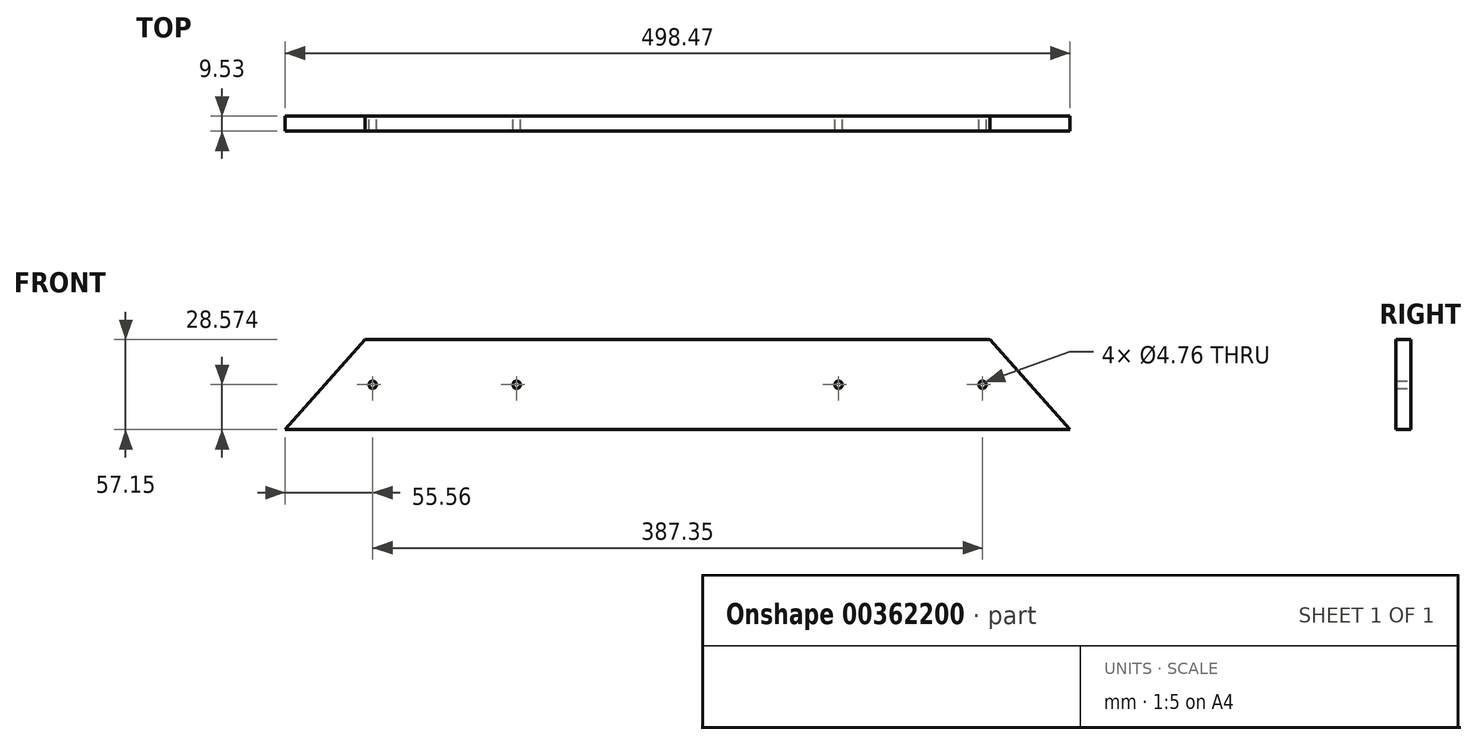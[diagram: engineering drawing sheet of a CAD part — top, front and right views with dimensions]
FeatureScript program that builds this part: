
annotation { "Feature Type Name" : "Feature", "Feature Type Description" : "" }
export const myFeature = defineFeature(function(context is Context, id is Id, definition is map)
    precondition{}
    {
        {
            var Q0;
            Q0=qCreatedBy(makeId("Front.planeOp"),FACE);
            var sketch = newSketch(context, id + "F0", { "sketchPlane" : qUnion([Q0])});
            skLineSegment(sketch, "E0.bottom", {"start": v(-185.67, -16.6) * mm, "end": v(211.2, -16.6) * mm});
            skLineSegment(sketch, "E0.top", {"start": v(-236.47, -73.75) * mm, "end": v(262, -73.75) * mm});
            skLineSegment(sketch, "E1", {"start": v(-236.47, -73.75) * mm, "end": v(-185.67, -16.6) * mm});
            skLineSegment(sketch, "E2", {"start": v(262, -73.75) * mm, "end": v(211.2, -16.6) * mm});
            skPoint(sketch, "E3.orphan", {"position": v(-211.39, -16.6) * mm});
            skPoint(sketch, "E0.right.start.orphan", {"position": v(261.69, -16.6) * mm});
            skLineSegment(sketch, "E4", {"start": v(211.2, -16.6) * mm, "end": v(211.2, -73.75) * mm, "construction": true});
            skLineSegment(sketch, "E5", {"start": v(211.2, -73.75) * mm, "end": v(119.13, -73.75) * mm});
            skLineSegment(sketch, "E6", {"start": v(-185.67, -16.6) * mm, "end": v(-185.67, -73.75) * mm, "construction": true});
            skLineSegment(sketch, "E7", {"start": v(-185.67, -73.75) * mm, "end": v(-93.6, -73.75) * mm});
            skLineSegment(sketch, "E8", {"start": v(119.13, -73.75) * mm, "end": v(119.13, -16.6) * mm, "construction": true});
            skLineSegment(sketch, "E9", {"start": v(-93.6, -73.75) * mm, "end": v(-93.6, -16.6) * mm, "construction": true});
            skPoint(sketch, "E10", {"position": v(119.13, -45.18) * mm});
            skPoint(sketch, "E11", {"position": v(-93.6, -45.18) * mm});
            skLineSegment(sketch, "E12", {"start": v(-176.15, -16.6) * mm, "end": v(-176.15, -73.75) * mm, "construction": true});
            skLineSegment(sketch, "E13", {"start": v(201.68, -16.6) * mm, "end": v(201.68, -73.75) * mm, "construction": true});
            skLineSegment(sketch, "E14", {"start": v(201.68, -45.18) * mm, "end": v(211.2, -45.18) * mm, "construction": true});
            skLineSegment(sketch, "E15", {"start": v(-185.67, -45.18) * mm, "end": v(-176.15, -45.18) * mm, "construction": true});
            skPoint(sketch, "E16", {"position": v(-180.91, -45.18) * mm});
            skLineSegment(sketch, "E17", {"start": v(110.87, -16.6) * mm, "end": v(110.87, -73.75) * mm, "construction": true});
            skLineSegment(sketch, "E18", {"start": v(-85.34, -16.6) * mm, "end": v(-85.34, -73.75) * mm, "construction": true});
            skLineSegment(sketch, "E19", {"start": v(-85.34, -45.18) * mm, "end": v(-93.6, -45.18) * mm, "construction": true});
            skLineSegment(sketch, "E20", {"start": v(119.13, -45.18) * mm, "end": v(110.87, -45.18) * mm, "construction": true});
            skPoint(sketch, "E21", {"position": v(115, -45.18) * mm});
            skPoint(sketch, "E22", {"position": v(-89.47, -45.18) * mm});
            skPoint(sketch, "E23", {"position": v(206.44, -45.18) * mm});
            skSolve(sketch);
        }
        {
            var Q0;
            Q0=makeQuery(id+"F0.imprint","IMPRINT",FACE,{"disambiguationData":[TD([[makeQuery(id+"F0.imprint","IMPRINT",EDGE,{"derivedFrom":sQuery(id+"F0.wireOp",EDGE,"E0.bottom")}),-1.0]])]});
            extrude(context, id + "F1", {"entities" : qUnion([Q0]), "depth" : 9.52 * mm});
        }
        {
            var Q0;
            Q0 = qSketchRegion(id + "F0", true);
            extrude(context, id + "F2", {"entities" : qUnion([Q0]), "operationType" : NewBodyOperationType.ADD, "depth" : 9.52 * mm});
        }
        {
            var Q0;
            Q0=sQuery(id+"F0.wireOp",VERTEX,"E21");
            var Q1;
            Q1=makeQuery(id+"F1.opExtrude","SWEPT_BODY",BODY,{"disambiguationData":[OSD([sQuery(id+"F0.wireOp",EDGE,"E0.bottom"),sQuery(id+"F0.wireOp",EDGE,"E0.top"),sQuery(id+"F0.wireOp",EDGE,"E1"),sQuery(id+"F0.wireOp",EDGE,"E2"),sQuery(id+"F0.wireOp",EDGE,"E5"),sQuery(id+"F0.wireOp",EDGE,"E7")])]});
            hole(context, id + "F3", {"style" : HoleStyle.SIMPLE, "endStyle" : HoleEndStyle.THROUGH, "oppositeDirection" : true, "holeDiameter" : 4.76 * mm, "isTappedThrough" : true, "tappedDepth" : 12.7 * mm, "tapClearance" : 3, "startFromSketch" : true, "locations" : qUnion([Q0]), "scope" : qUnion([Q1])});
        }
        {
            var Q0;
            Q0=sQuery(id+"F0.wireOp",VERTEX,"E22");
            var Q1;
            Q1=makeQuery(id+"F1.opExtrude","SWEPT_BODY",BODY,{"disambiguationData":[OSD([sQuery(id+"F0.wireOp",EDGE,"E0.bottom"),sQuery(id+"F0.wireOp",EDGE,"E0.top"),sQuery(id+"F0.wireOp",EDGE,"E1"),sQuery(id+"F0.wireOp",EDGE,"E2"),sQuery(id+"F0.wireOp",EDGE,"E5"),sQuery(id+"F0.wireOp",EDGE,"E7")])]});
            hole(context, id + "F4", {"style" : HoleStyle.SIMPLE, "endStyle" : HoleEndStyle.THROUGH, "oppositeDirection" : true, "holeDiameter" : 4.76 * mm, "isTappedThrough" : true, "tappedDepth" : 12.7 * mm, "tapClearance" : 3, "startFromSketch" : true, "locations" : qUnion([Q0]), "scope" : qUnion([Q1])});
        }
        {
            var Q0;
            Q0=sQuery(id+"F0.wireOp",VERTEX,"E23");
            var Q1;
            Q1=makeQuery(id+"F1.opExtrude","SWEPT_BODY",BODY,{"disambiguationData":[OSD([sQuery(id+"F0.wireOp",EDGE,"E0.bottom"),sQuery(id+"F0.wireOp",EDGE,"E0.top"),sQuery(id+"F0.wireOp",EDGE,"E1"),sQuery(id+"F0.wireOp",EDGE,"E2"),sQuery(id+"F0.wireOp",EDGE,"E5"),sQuery(id+"F0.wireOp",EDGE,"E7")])]});
            hole(context, id + "F5", {"style" : HoleStyle.SIMPLE, "endStyle" : HoleEndStyle.THROUGH, "oppositeDirection" : true, "holeDiameter" : 4.76 * mm, "isTappedThrough" : true, "tappedDepth" : 12.7 * mm, "tapClearance" : 3, "startFromSketch" : true, "locations" : qUnion([Q0]), "scope" : qUnion([Q1])});
        }
        {
            var Q0;
            Q0=sQuery(id+"F0.wireOp",VERTEX,"E16");
            var Q1;
            Q1=makeQuery(id+"F1.opExtrude","SWEPT_BODY",BODY,{"disambiguationData":[OSD([sQuery(id+"F0.wireOp",EDGE,"E0.bottom"),sQuery(id+"F0.wireOp",EDGE,"E0.top"),sQuery(id+"F0.wireOp",EDGE,"E1"),sQuery(id+"F0.wireOp",EDGE,"E2"),sQuery(id+"F0.wireOp",EDGE,"E5"),sQuery(id+"F0.wireOp",EDGE,"E7")])]});
            hole(context, id + "F6", {"style" : HoleStyle.SIMPLE, "endStyle" : HoleEndStyle.THROUGH, "oppositeDirection" : true, "holeDiameter" : 4.76 * mm, "isTappedThrough" : true, "tappedDepth" : 12.7 * mm, "tapClearance" : 3, "startFromSketch" : true, "locations" : qUnion([Q0]), "scope" : qUnion([Q1])});
        }
    });
